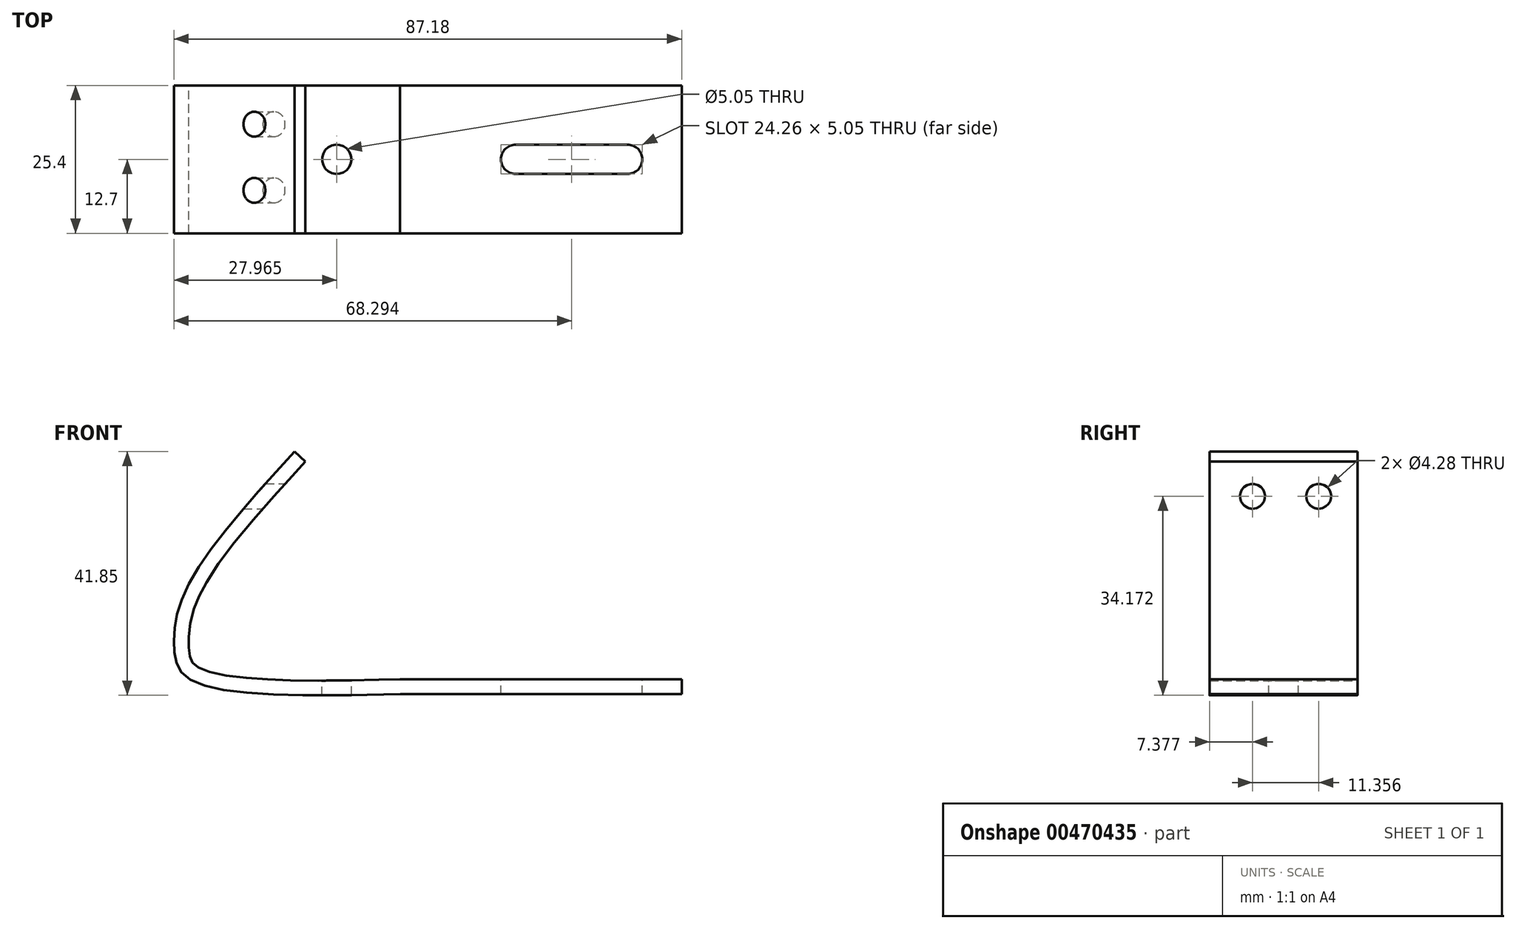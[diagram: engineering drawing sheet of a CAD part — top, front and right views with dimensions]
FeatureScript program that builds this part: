
annotation { "Feature Type Name" : "Feature", "Feature Type Description" : "" }
export const myFeature = defineFeature(function(context is Context, id is Id, definition is map)
    precondition{}
    {
        {
            var Q0;
            Q0=qCreatedBy(makeId("Front.planeOp"),FACE);
            var sketch = newSketch(context, id + "F0", { "sketchPlane" : qUnion([Q0])});
            skLineSegment(sketch, "E0", {"start": v(48.3, 0) * mm, "end": v(0, 0) * mm});
            skFitSpline(sketch, "E1", {"points": [v(0, 0) * mm, v(-36.2, 2.55) * mm, v(-38.84, 7.82) * mm, v(-36.8, 17.95) * mm, v(-18.17, 41.66) * mm], "startDerivative": vector(-132.5, -2.7) * mm, "endDerivative": vector(72.36, 79.5) * mm});
            skFitSpline(sketch, "E2.0", {"points": [v(-0.05, 2.54) * mm, v(-2.81, 2.48) * mm, v(-8.32, 2.37) * mm, v(-14.89, 2.33) * mm, v(-19.76, 2.41) * mm, v(-23.18, 2.55) * mm, v(-26.32, 2.77) * mm, v(-29.1, 3.09) * mm, v(-31.5, 3.5) * mm, v(-33.1, 3.93) * mm, v(-34.1, 4.3) * mm, v(-34.68, 4.6) * mm, v(-35.1, 4.85) * mm, v(-35.4, 5.1) * mm, v(-35.62, 5.33) * mm, v(-35.78, 5.58) * mm, v(-35.92, 5.85) * mm, v(-36.04, 6.18) * mm, v(-36.14, 6.6) * mm, v(-36.22, 7.08) * mm, v(-36.28, 7.64) * mm, v(-36.32, 8.27) * mm, v(-36.34, 8.91) * mm, v(-36.33, 9.8) * mm, v(-36.26, 10.93) * mm, v(-36.05, 12.37) * mm, v(-35.68, 13.9) * mm, v(-35.21, 15.26) * mm, v(-34.73, 16.4) * mm, v(-34.17, 17.58) * mm, v(-33.3, 19.16) * mm, v(-31.6, 21.85) * mm, v(-28.93, 25.48) * mm, v(-25.09, 30.14) * mm, v(-20.8, 34.99) * mm, v(-17.8, 38.29) * mm, v(-16.29, 39.95) * mm]});
            skLineSegment(sketch, "E3", {"start": v(-0.05, 2.54) * mm, "end": v(48.3, 2.54) * mm});
            skLineSegment(sketch, "E4", {"start": v(48.3, 2.54) * mm, "end": v(48.3, 0) * mm});
            skLineSegment(sketch, "E5", {"start": v(-16.29, 39.95) * mm, "end": v(-18.17, 41.66) * mm});
            skSolve(sketch);
        }
        {
            var Q0;
            Q0=qSketchRegion(id+"F0",true);
            extrude(context, id + "F1", {"entities" : qUnion([Q0]), "depth" : 25.4 * mm, "symmetric" : true});
        }
        {
            var Q0;
            Q0=makeQuery(id+"F1.opExtrude","SWEPT_FACE",FACE,{"disambiguationData":[OSD([sQuery(id+"F0.wireOp",EDGE,"E3")])]});
            var sketch = newSketch(context, id + "F2", { "sketchPlane" : qUnion([Q0])});
            skArc(sketch, "E6", {"start": v(39.02, -2.53) * mm, "mid": v(41.55, 0) * mm, "end": v(39.02, 2.53) * mm});
            skArc(sketch, "E7", {"start": v(19.8, 2.53) * mm, "mid": v(17.28, 0) * mm, "end": v(19.8, -2.53) * mm});
            skCircle(sketch, "E8", {"center": v(-10.92, 0) * mm, "radius": 2.53 * mm});
            skLineSegment(sketch, "E9", {"start": v(19.8, -2.53) * mm, "end": v(39.02, -2.53) * mm});
            skLineSegment(sketch, "E10", {"start": v(19.8, 2.53) * mm, "end": v(39.02, 2.53) * mm});
            skSolve(sketch);
        }
        {
            var Q0;
            Q0=qSketchRegion(id+"F2",true);
            extrude(context, id + "F3", {"entities" : qUnion([Q0]), "operationType" : NewBodyOperationType.REMOVE, "oppositeDirection" : true, "depth" : 25.4 * mm});
        }
        {
            var Q0;
            Q0=qCreatedBy(makeId("Right.planeOp"),FACE);
            var sketch = newSketch(context, id + "F4", { "sketchPlane" : qUnion([Q0])});
            skCircle(sketch, "E11", {"center": v(6.03, 33.98) * mm, "radius": 2.14 * mm});
            skCircle(sketch, "E12", {"center": v(-5.32, 33.98) * mm, "radius": 2.14 * mm});
            skSolve(sketch);
        }
        {
            var Q0;
            Q0=qSketchRegion(id+"F4",true);
            extrude(context, id + "F5", {"entities" : qUnion([Q0]), "operationType" : NewBodyOperationType.REMOVE, "oppositeDirection" : true, "depth" : 40.44 * mm});
        }
    });
